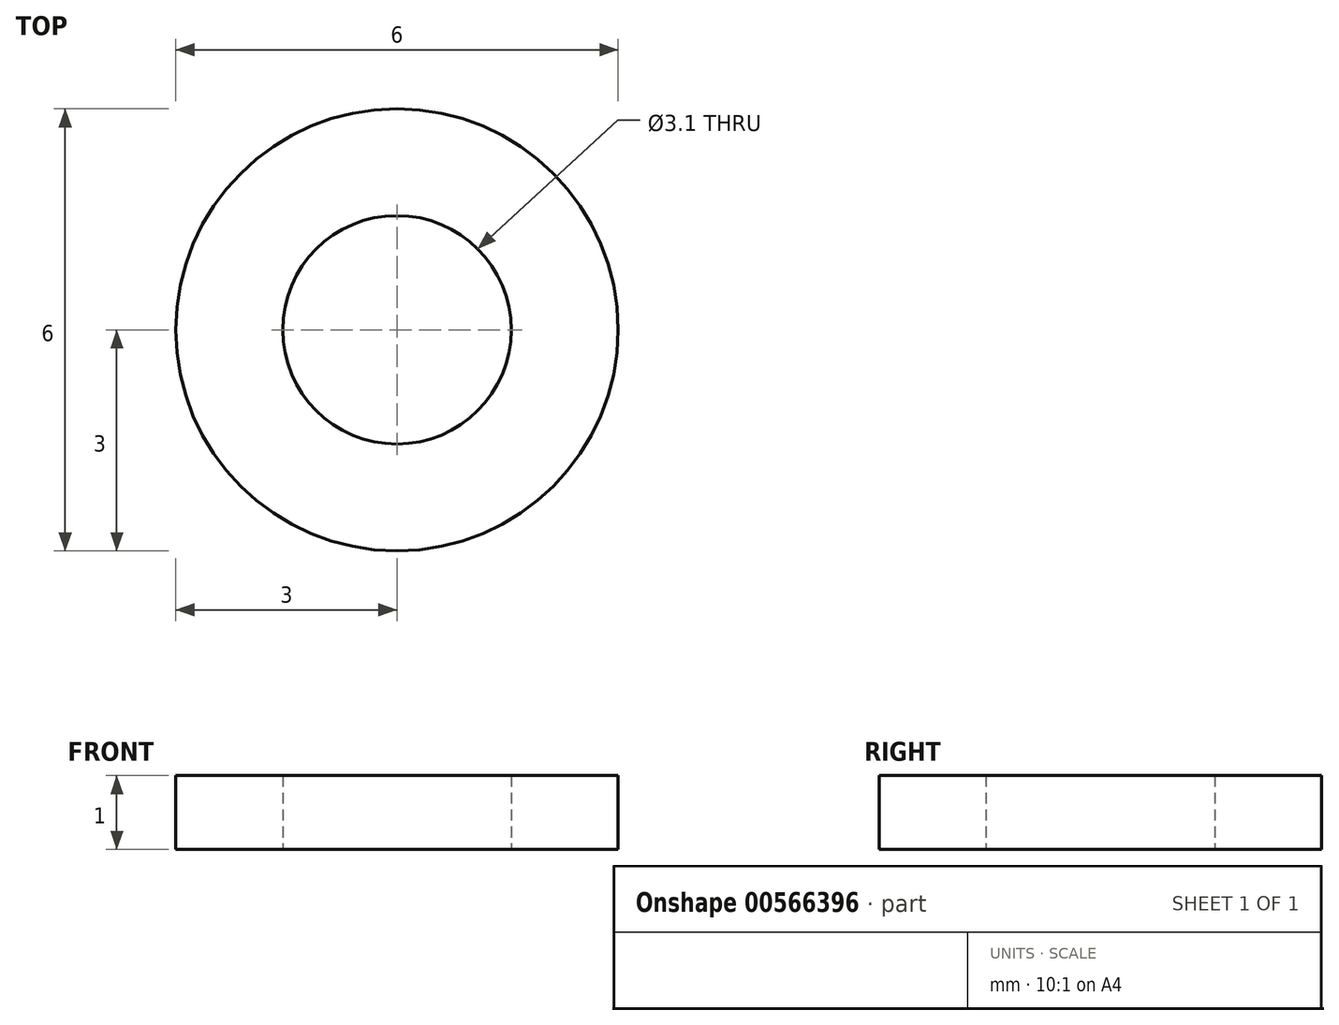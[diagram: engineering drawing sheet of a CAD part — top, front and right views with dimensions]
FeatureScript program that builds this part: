
annotation { "Feature Type Name" : "Feature", "Feature Type Description" : "" }
export const myFeature = defineFeature(function(context is Context, id is Id, definition is map)
    precondition{}
    {
        {
            var Q0;
            Q0=qCreatedBy(makeId("Top.planeOp"),FACE);
            var sketch = newSketch(context, id + "F0", { "sketchPlane" : qUnion([Q0])});
            skCircle(sketch, "E0", {"center": v(0, 0) * mm, "radius": 1.55 * mm});
            skCircle(sketch, "E1", {"center": v(0, 0) * mm, "radius": 3 * mm});
            skSolve(sketch);
        }
        {
            var Q0;
            Q0=qSketchRegion(id+"F0",true);
            extrude(context, id + "F1", {"entities" : qUnion([Q0]), "depth" : 1 * mm, "offsetDistance" : 25 * mm});
        }
    });
